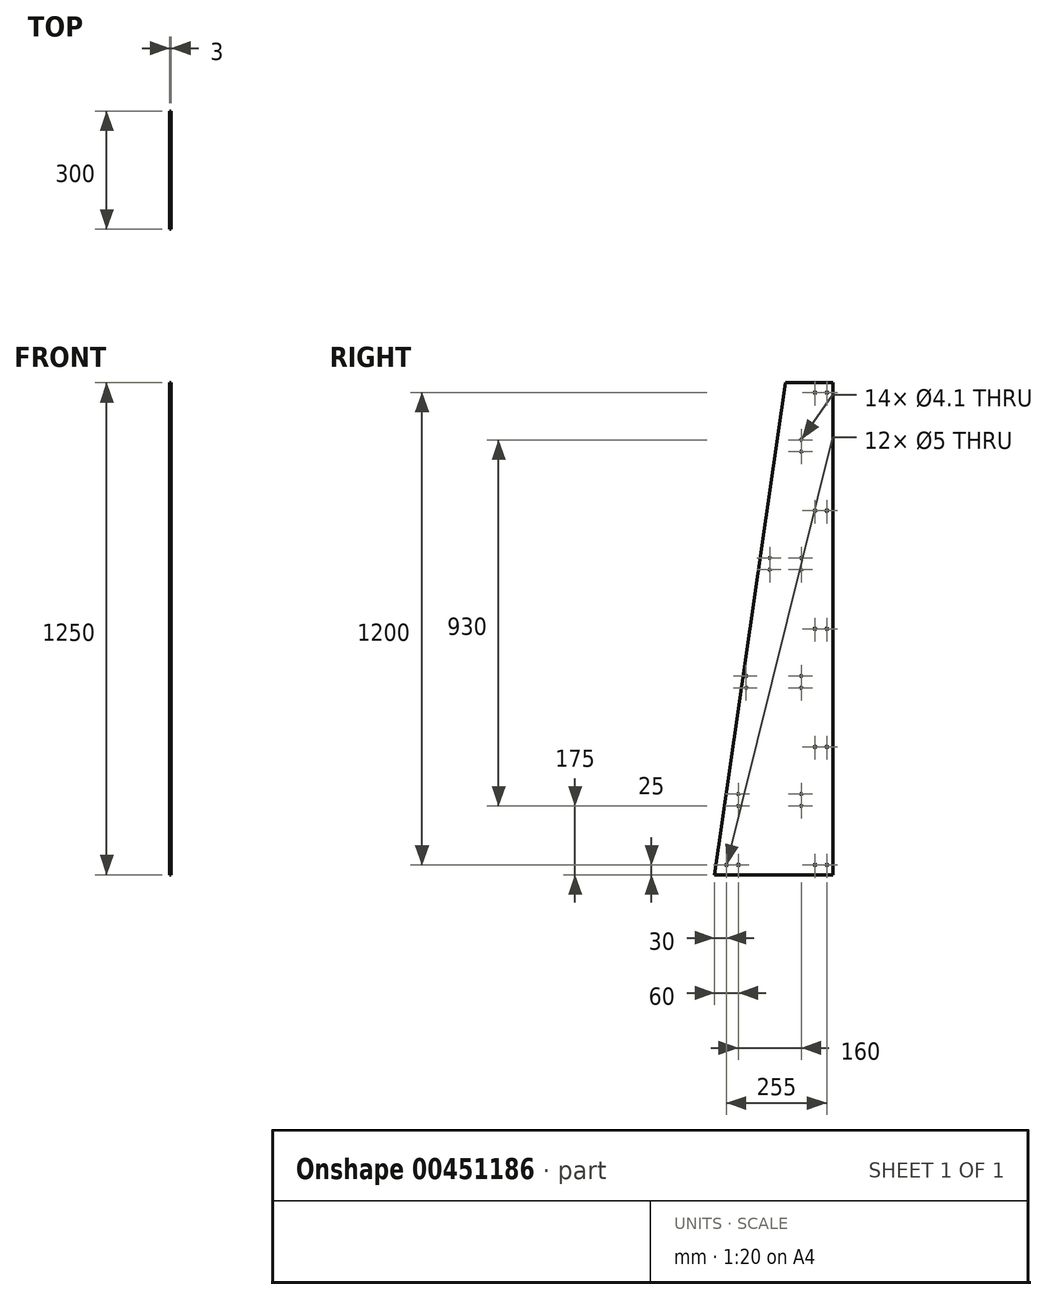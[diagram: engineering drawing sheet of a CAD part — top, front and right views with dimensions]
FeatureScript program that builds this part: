
annotation { "Feature Type Name" : "Feature", "Feature Type Description" : "" }
export const myFeature = defineFeature(function(context is Context, id is Id, definition is map)
    precondition{}
    {
        {
            var Q0;
            Q0=qCreatedBy(makeId("Right.planeOp"),FACE);
            var sketch = newSketch(context, id + "F0", { "sketchPlane" : qUnion([Q0])});
            skLineSegment(sketch, "E0", {"start": v(-740.64, 1250) * mm, "end": v(-860.64, 1250) * mm});
            skLineSegment(sketch, "E1", {"start": v(-860.64, 1250) * mm, "end": v(-1040.64, 0) * mm});
            skLineSegment(sketch, "E2", {"start": v(-1040.64, 0) * mm, "end": v(-740.64, 0) * mm});
            skLineSegment(sketch, "E3", {"start": v(-740.64, 0) * mm, "end": v(-740.64, 1250) * mm});
            skSolve(sketch);
        }
        {
            var Q0;
            Q0 = qSketchRegion(id + "F0", true);
            extrude(context, id + "F1", {"entities" : qUnion([Q0]), "depth" : 3 * mm, "offsetDistance" : 25 * mm});
        }
        {
            var Q0;
            Q0=makeQuery(id+"F1.opExtrude","CAP_FACE",FACE,{"disambiguationData":[OSD([sQuery(id+"F0.wireOp",EDGE,"E0"),sQuery(id+"F0.wireOp",EDGE,"E1"),sQuery(id+"F0.wireOp",EDGE,"E2"),sQuery(id+"F0.wireOp",EDGE,"E3")])],"isStart":true});
            var sketch = newSketch(context, id + "F2", { "sketchPlane" : qUnion([Q0])});
            skCircle(sketch, "E4", {"center": v(755.64, 25) * mm, "radius": 2.5 * mm});
            skCircle(sketch, "E5", {"center": v(785.64, 25) * mm, "radius": 2.5 * mm});
            skCircle(sketch, "E6.0.1.0", {"center": v(755.64, 325) * mm, "radius": 2.5 * mm});
            skCircle(sketch, "E6.0.1.1", {"center": v(785.64, 325) * mm, "radius": 2.5 * mm});
            skCircle(sketch, "E6.0.2.0", {"center": v(755.64, 625) * mm, "radius": 2.5 * mm});
            skCircle(sketch, "E6.0.2.1", {"center": v(785.64, 625) * mm, "radius": 2.5 * mm});
            skCircle(sketch, "E6.0.3.0", {"center": v(755.64, 925) * mm, "radius": 2.5 * mm});
            skCircle(sketch, "E6.0.3.1", {"center": v(785.64, 925) * mm, "radius": 2.5 * mm});
            skCircle(sketch, "E6.0.4.0", {"center": v(755.64, 1225) * mm, "radius": 2.5 * mm});
            skCircle(sketch, "E6.0.4.1", {"center": v(785.64, 1225) * mm, "radius": 2.5 * mm});
            skLineSegment(sketch, "E6.direction1", {"start": v(720.64, 25) * mm, "end": v(755.64, 25) * mm, "construction": true});
            skLineSegment(sketch, "E6.direction2", {"start": v(755.64, 25) * mm, "end": v(755.64, 325) * mm, "construction": true});
            skCircle(sketch, "E7", {"center": v(820.64, 175) * mm, "radius": 2.05 * mm});
            skCircle(sketch, "E8", {"center": v(820.64, 205) * mm, "radius": 2.05 * mm});
            skPoint(sketch, "E9", {"position": v(800.64, 1250) * mm});
            skCircle(sketch, "E10.0.1.0", {"center": v(820.64, 505) * mm, "radius": 2.05 * mm});
            skCircle(sketch, "E10.0.1.1", {"center": v(820.64, 475) * mm, "radius": 2.05 * mm});
            skCircle(sketch, "E10.0.2.0", {"center": v(820.64, 805) * mm, "radius": 2.05 * mm});
            skCircle(sketch, "E10.0.2.1", {"center": v(820.64, 775) * mm, "radius": 2.05 * mm});
            skCircle(sketch, "E10.0.3.0", {"center": v(820.64, 1105) * mm, "radius": 2.05 * mm});
            skCircle(sketch, "E10.0.3.1", {"center": v(820.64, 1075) * mm, "radius": 2.05 * mm});
            skLineSegment(sketch, "E10.direction1", {"start": v(774.58, 175) * mm, "end": v(820.64, 175) * mm, "construction": true});
            skLineSegment(sketch, "E10.direction2", {"start": v(820.64, 175) * mm, "end": v(820.64, 475) * mm, "construction": true});
            skCircle(sketch, "E11", {"center": v(980.64, 25) * mm, "radius": 2.5 * mm});
            skCircle(sketch, "E12", {"center": v(1010.64, 25) * mm, "radius": 2.5 * mm});
            skCircle(sketch, "E13", {"center": v(980.64, 175) * mm, "radius": 2.05 * mm});
            skCircle(sketch, "E14", {"center": v(980.64, 205) * mm, "radius": 2.05 * mm});
            skCircle(sketch, "E15", {"center": v(960.64, 475) * mm, "radius": 2.05 * mm});
            skCircle(sketch, "E16", {"center": v(960.64, 505) * mm, "radius": 2.05 * mm});
            skCircle(sketch, "E17", {"center": v(900.64, 775) * mm, "radius": 2.05 * mm});
            skCircle(sketch, "E18", {"center": v(900.64, 805) * mm, "radius": 2.05 * mm});
            skSolve(sketch);
        }
        {
            var Q0;
            Q0 = qSketchRegion(id + "F2", true);
            extrude(context, id + "F3", {"entities" : qUnion([Q0]), "operationType" : NewBodyOperationType.REMOVE, "oppositeDirection" : true, "depth" : 25 * mm, "offsetDistance" : 25 * mm});
        }
    });
